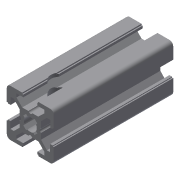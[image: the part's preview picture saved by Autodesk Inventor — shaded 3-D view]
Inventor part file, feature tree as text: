
AUTODESK INVENTOR PART (.ipt)
format: ipt  version: 2013 (Build 170138000, 138)  size: 247,296 bytes
history: native  units: in
note: dims shown in document units (in); Inventor stores cm internally (conversion verified against a paired STEP export)
features: plane x3, sketch x2, extrude x1, hole x1
ambient origin geometry x8: Origin, YZ Plane, XZ Plane, XY Plane, X Axis, Y Axis, Z Axis, Center Point
bodies: Solid1 (feature_tree)
feature tree (7):
  extrude  "Extrusion1"  [1 undecoded]
  plane  "Work Plane1"
  plane  "Work Plane2"
  plane  "Work Plane3"
  hole  "Hole1"  [1 undecoded]
  sketch  "Sketch1"  dims[d0=2.0in d1=0.0in d2=-0.5in]
  sketch  "Sketch2"  dims[d5=0.309in d6=0.75in d7=0.375in d8=0.25in d9=0.5635in d10=1.0in d11=0.8108in]
note: 2 required parameter values undecoded (feature->parameter linkage not recoverable at this tier; creation-order binding heuristic only, values carry confidence <= 0.55)
